AUTODESK INVENTOR PART (.ipt)
format: ipt  version: 2021.3 (Build 253353000, 353)  size: 214,016 bytes
history: imported  units: in
note: dims shown in document units (in); Inventor stores cm internally (conversion verified against a paired STEP export)
features: imported_body x1
ambient origin geometry x8: Origin, YZ Plane, XZ Plane, XY Plane, X Axis, Y Axis, Z Axis, Center Point
bodies: Solid1 (imported_parasolid), Solid2 (imported_parasolid), Solid3 (imported_parasolid), Solid4 (imported_parasolid), Solid5 (imported_parasolid), Solid6 (imported_parasolid), Solid7 (imported_parasolid), Solid8 (imported_parasolid), Solid9 (imported_parasolid), Solid10 (imported_parasolid), Solid11 (imported_parasolid), Solid12 (imported_parasolid), Solid13 (imported_parasolid), Solid14 (imported_parasolid), Solid15 (imported_parasolid), Solid16 (imported_parasolid), Body1 (imported_parasolid), Body2 (imported_parasolid), Body3 (imported_parasolid), Body4 (imported_parasolid), Body5 (imported_parasolid), Body6 (imported_parasolid), Body7 (imported_parasolid), Body8 (imported_parasolid), Body9 (imported_parasolid), Body10 (imported_parasolid), Body11 (imported_parasolid), Body12 (imported_parasolid), Body13 (imported_parasolid), Body14 (imported_parasolid), Body15 (imported_parasolid), Body16 (imported_parasolid)
feature tree (1):
  imported_body  NMx_Import_Brep_tag  [imported B-rep: ~215 faces, bbox_mm=[6.4, 1.2, 5.0]]
